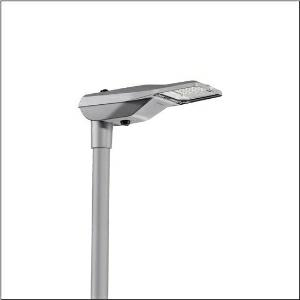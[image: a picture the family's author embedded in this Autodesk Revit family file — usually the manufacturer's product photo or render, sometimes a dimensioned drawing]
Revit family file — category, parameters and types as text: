
# Revit family: streetlight_sl_21_iq_micro___stw1_0a_5xe1e31y08db_aea3
name_source: partatom
category: Lighting Fixtures
units: mm (PartAtom-declared; Revit-internal decimal feet)

## family parameters
Cut with Voids When Loaded = No
Host = Face
Light Source = No
Part Type = Normal
Room Calculation Point = No
Round Connector Dimension = Use Diameter
Shared = No

## types (1)
- --- (1 x LED, 5110 lm, 39.1 W, 3000K)
    Apparent Load = 39 VA
    CIE Flux Codes = 38 75 98 100 100
    Color Rendering = 70
    Color Temperature = 3000K
    Default Elevation = 1800 mm
    Description = Streetlight SL 21 iQ micro, mast luminaire, primary light control with lens, of PMMA, primary optical cover: cover, of toughened safety glass, transparent, light distribution: STW1.0a, light emission: direct distribution, primary light characteristic: asymmetric, installation type: post-top, side-entry, LED, High Power LED, rated luminous flux: 5.110lm, luminous efficacy: 131lm/W, light colour: 730, colour temperature: 3000K, control gear: iQ-Street Remote, D4i with power reduction, control: pre-setting: logarithmic dimming characteristic, Street-Remote, Auto-Match, Temp-Guard, Lumen-Switch, Night-Set, Smart-Wire, Light-Fading, Desk-Remote (wireless, voltage-free reading and setting of iQ features in the workshop via application-optimized NFC function/RFID function), optimised constant luminous flux control (CLO 2.0), mains connection: 220..240V, AC, 50/60Hz, start of lifetime: 39W, end of service life: 41W, reduction: 17W, luminaire housing, of diecast aluminium, powder-coated, SITECO metallic grey (DB 702S), corrosivity category C5 high according to DIN EN ISO 12944, please order mast flange separately, inclination adjustable: 0°, 5°, 10°, 15°, sealing non-destructively replaceable, multi-level sealing system, length: 528mm, width: 235mm, height: 110mm, mast flange for spigot size: 42mm (side-entry): 5XC10008XM4, 60/48mm (side-entry/post-top): 5XC10108XM2, 76/60mm (side-entry/post-top): 5XC10108XM1, mounting height: 4..8m, Smart Interface below and above, protection rating (complete): IP66, insulation class (complete): insulation class II (safety insulation), certification: CE, ENEC, ENEC+, VDE, impact resistance: IK10, permissible operating ambient temperature for outdoor applications: -40..+50°C, standard-compliant lighting for roads and squares, packaging unit: 1 piece

Light Distribution: STW1.0a
    Height = 110 mm
    Lamp = 1 x LED
    Lamp Light Flux = 5110 lm
    Lamp Power = 39.1 W
    Lamp count = 1
    Length = 528 mm
    Luminous efficacy = 131 lm/W
    Manufacturer = Siteco
    ModVariant = No
    Model = 5XE1E31Y08DB
    Number of Poles = 1
    OnlyDefault = Yes
    Power Factor = 1
    Product Name = Streetlight SL 21 iQ micro | STW1.0a
    Product group = mast luminaire | pylon top
    ProductGroupID = 6100
    Protection Class = Protection class II
    Protection Degree = IP 66
    RLX_Detail_Level = 1
    RLX_Emergency_Light_Flux = 0 lm
    RLX_Emergency_Type = 0
    RLX_Emergency_Type_DB = No
    RlxData = <blob elided: 98517 chars, md5=47e6874a>
    Socket = socket
    Standby Power = 0 W
    System Light Flux = 5110 lm
    System Power = 39 W
    Type Comments = factory setting: luminous flux: 100 % | dim-lin: 254 | 765 mA
    Type Image = l_1007239.jpg
    URL = http://relux.com
    VarID = @adj_114501
    Voltage = 0 V
    Weight = 0.00 kg
    Width = 235 mm

## geometry (parser evidence)
native form markers: Blend x4, Sweep x11
no freeform markers — native parametric forms only
